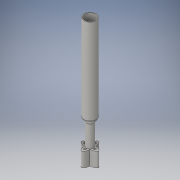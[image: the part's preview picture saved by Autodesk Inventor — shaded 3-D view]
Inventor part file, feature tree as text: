
AUTODESK INVENTOR PART (.ipt)
format: ipt  version: 2016 (Build 200138000, 138)  size: 160,768 bytes
history: native  units: in
note: dims shown in document units (in); Inventor stores cm internally (conversion verified against a paired STEP export)
features: sketch x9, extrude x5, fillet x2, hole x1
ambient origin geometry x8: Origin, YZ Plane, XZ Plane, XY Plane, X Axis, Y Axis, Z Axis, Center Point
bodies: Solid1 (feature_tree)
feature tree (17):
  sketch  "Sketch1"  dims[d0=0.4646in d1=0.1693in]
  sketch  "Sketch2"  dims[d2=0.4646in d3=0.1693in]
  extrude  "Extrusion1"  Depth=0.4646in
  hole  "Hole1"  [1 undecoded]
  extrude  "Extrusion3"  Depth=0.1181in
  sketch  "Sketch6"  dims[d6=0.1181in d7=0.1181in d8=0.2756in]
  extrude  "Extrusion4"  Depth=0.1181in
  fillet  "Fillet1"  Radius=0.2756in
  sketch  "Sketch8"  dims[d11=0.2756in d14=0.7874in d15=0.0in]
  sketch  "Sketch9"  dims[d16=0.1181in d17=0.2362in d18=0.1575in d19=0.0787in d20=90.0deg d21=0.7874in d22=0.8108in d25=0.3937in]
  extrude  "Extrusion5"  Depth=0.2756in
  extrude  "Extrusion6"  Depth=0.7874in TaperAngle=0.0deg
  sketch  "Sketch10"  dims[d26=0.2362in]
  sketch  "Sketch11"  dims[d27=1.1811in d28=0.0in d29=0.6299in d30=0.1969in d31=0.0in d32=0.2662in d33=0.6693in d34=0.5906in d35=0.4528in d36=0.374in d37=4.7244in d38=0.0in d39=0.7874in d40=0.0in d43=0.0787in d44=0.0394in d45=0.0394in]
  fillet  "Fillet4"  Radius=0.3937in
  sketch  "Sketch5"  dims[d4=0.1181in d5=0.1181in]
  sketch  "Sketch7"  dims[d9=0.2756in d10=0.2756in]
note: 1 required parameter value undecoded (feature->parameter linkage not recoverable at this tier; creation-order binding heuristic only, values carry confidence <= 0.55)
